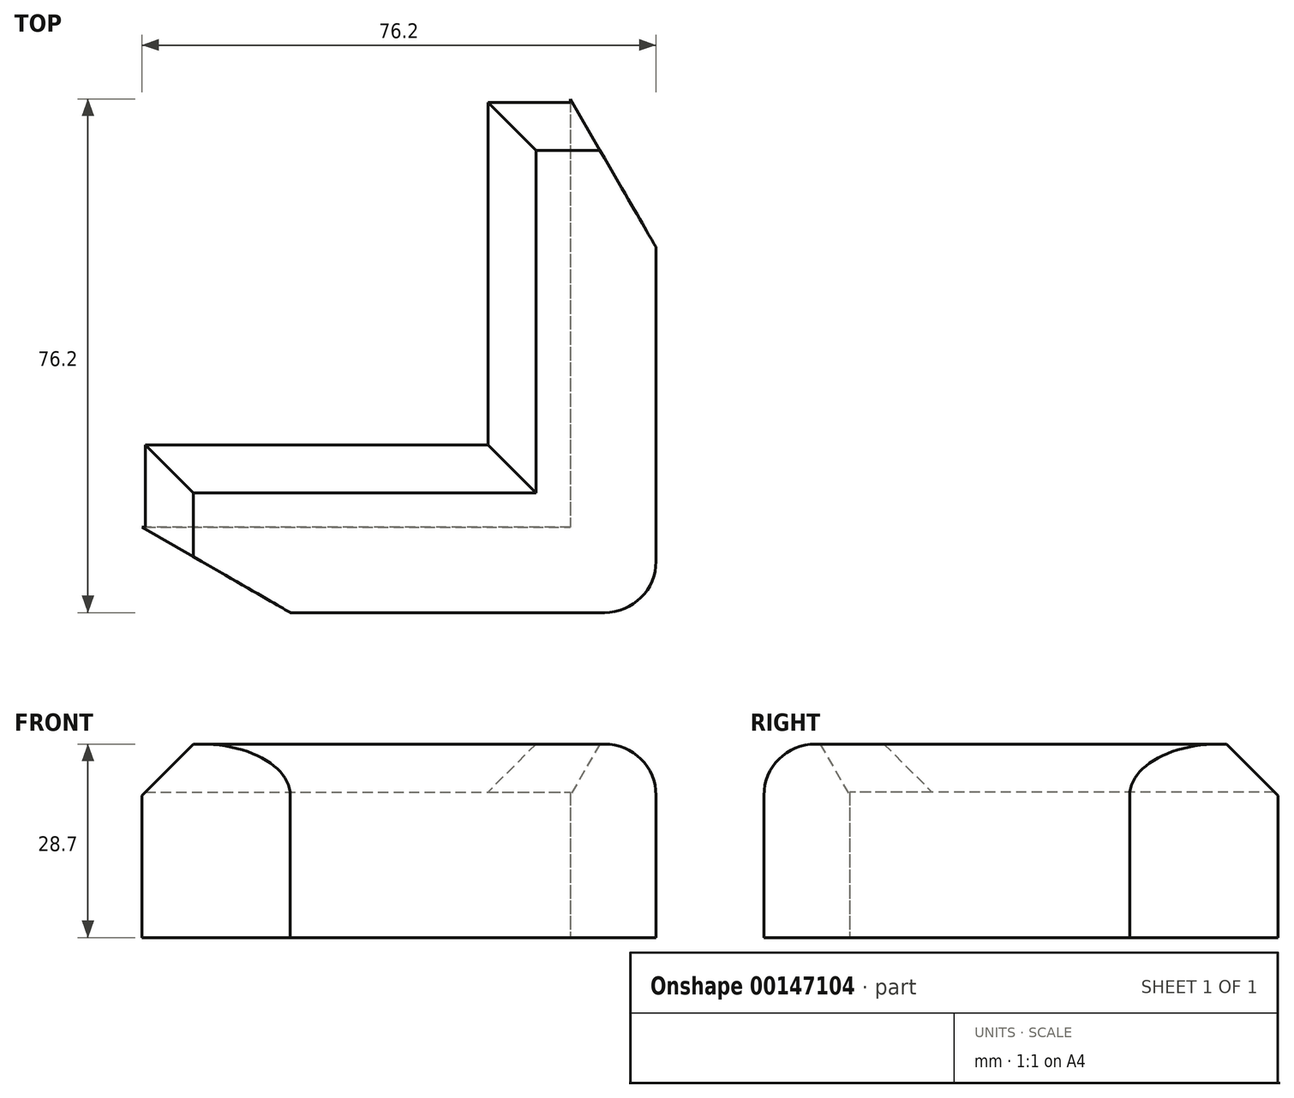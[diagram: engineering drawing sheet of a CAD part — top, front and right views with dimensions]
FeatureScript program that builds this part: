
annotation { "Feature Type Name" : "Feature", "Feature Type Description" : "" }
export const myFeature = defineFeature(function(context is Context, id is Id, definition is map)
    precondition{}
    {
        {
            var Q0;
            Q0=qCreatedBy(makeId("Front.planeOp"),FACE);
            var sketch = newSketch(context, id + "F0", { "sketchPlane" : qUnion([Q0])});
            skLineSegment(sketch, "E0.bottom", {"start": v(38.1, 14.35) * mm, "end": v(-38.1, 14.35) * mm});
            skLineSegment(sketch, "E0.top", {"start": v(38.1, -14.35) * mm, "end": v(-38.1, -14.35) * mm});
            skLineSegment(sketch, "E0.left", {"start": v(38.1, 14.35) * mm, "end": v(38.1, -14.35) * mm});
            skLineSegment(sketch, "E0.right", {"start": v(-38.1, 14.35) * mm, "end": v(-38.1, -14.35) * mm});
            skPoint(sketch, "E0.middle", {"position": v(0, 0) * mm});
            skLineSegment(sketch, "E1", {"start": v(25.4, 14.35) * mm, "end": v(25.4, -14.35) * mm});
            skLineSegment(sketch, "E2", {"start": v(-38.1, 7.24) * mm, "end": v(38.1, 7.24) * mm});
            skLineSegment(sketch, "E3", {"start": v(12.7, 14.35) * mm, "end": v(12.7, 7.24) * mm});
            skSolve(sketch);
        }
        {
            var Q0;
            {var subQ0=sQuery(id+"F0.wireOp",EDGE,"E0.right");var subQ1=sQuery(id+"F0.wireOp",EDGE,"E0.top");var subQ2=makeQuery(id+"F0.imprint","INTERSECT",VERTEX,{"derivedFrom":[subQ1,subQ0]});Q0=makeQuery(id+"F0.imprint","IMPRINT",FACE,{"disambiguationData":[TD([[makeQuery(id+"F0.imprint","IMPRINT",EDGE,{"disambiguationData":[TD([[subQ2,1.0]])],"derivedFrom":subQ1}),-1.0]])]});}
            extrude(context, id + "F1", {"entities" : qUnion([Q0]), "oppositeDirection" : true, "depth" : 12.7 * mm});
        }
        {
            var Q0;
            {var subQ0=sQuery(id+"F0.wireOp",EDGE,"E0.right");var subQ1=sQuery(id+"F0.wireOp",EDGE,"E0.bottom");var subQ2=makeQuery(id+"F0.imprint","INTERSECT",VERTEX,{"derivedFrom":[subQ1,subQ0]});Q0=makeQuery(id+"F0.imprint","IMPRINT",FACE,{"disambiguationData":[TD([[makeQuery(id+"F0.imprint","IMPRINT",EDGE,{"disambiguationData":[TD([[subQ2,1.0]])],"derivedFrom":subQ1}),1.0]])]});}
            extrude(context, id + "F2", {"entities" : qUnion([Q0]), "operationType" : NewBodyOperationType.ADD, "oppositeDirection" : true, "depth" : 25.4 * mm});
        }
        {
            var Q0;
            {var subQ0=sQuery(id+"F0.wireOp",EDGE,"E0.left");var subQ1=sQuery(id+"F0.wireOp",EDGE,"E0.top");var subQ2=makeQuery(id+"F0.imprint","INTERSECT",VERTEX,{"derivedFrom":[subQ1,subQ0]});Q0=makeQuery(id+"F0.imprint","IMPRINT",FACE,{"disambiguationData":[TD([[makeQuery(id+"F0.imprint","IMPRINT",EDGE,{"disambiguationData":[TD([[subQ2,-1.0]])],"derivedFrom":subQ1}),-1.0]])]});}
            var Q1;
            {var subQ0=sQuery(id+"F0.wireOp",EDGE,"E0.left");var subQ1=sQuery(id+"F0.wireOp",EDGE,"E0.bottom");var subQ2=makeQuery(id+"F0.imprint","INTERSECT",VERTEX,{"derivedFrom":[subQ1,subQ0]});Q1=makeQuery(id+"F0.imprint","IMPRINT",FACE,{"disambiguationData":[TD([[makeQuery(id+"F0.imprint","IMPRINT",EDGE,{"disambiguationData":[TD([[subQ2,-1.0]])],"derivedFrom":subQ1}),1.0]])]});}
            extrude(context, id + "F3", {"entities" : qUnion([Q0, Q1]), "operationType" : NewBodyOperationType.ADD, "oppositeDirection" : true, "depth" : 76.2 * mm});
        }
        {
            var Q0;
            {var subQ3=sQuery(id+"F0.wireOp",EDGE,"E3");Q0=makeQuery(id+"F0.imprint","IMPRINT",FACE,{"disambiguationData":[TD([[makeQuery(id+"F0.imprint","IMPRINT",EDGE,{"derivedFrom":subQ3}),1.0]])]});}
            extrude(context, id + "F4", {"entities" : qUnion([Q0]), "operationType" : NewBodyOperationType.ADD, "oppositeDirection" : true, "depth" : 76.2 * mm});
        }
        {
            var Q0;
            Q0=makeQuery(id+"F3.opExtrude","CAP_EDGE",EDGE,{"disambiguationData":[OSD([sQuery(id+"F0.wireOp",EDGE,"E0.left")])],"isStart":false});
            chamfer(context, id + "F5", {"entities" : qUnion([Q0]), "chamferType" : ChamferType.OFFSET_ANGLE, "width" : 12.7 * mm, "oppositeDirection" : false, "angle" : 60 * degree, "tangentPropagation" : true});
        }
        {
            var Q0;
            {var subQ0=sQuery(id+"F0.wireOp",EDGE,"E0.right");Q0=makeQuery(id+"F2.boolean.opBoolean","MERGE",EDGE,{"derivedFrom":[makeQuery(id+"F1.opExtrude","CAP_EDGE",EDGE,{"disambiguationData":[OSD([subQ0])],"isStart":true}),makeQuery(id+"F2.opExtrude","CAP_EDGE",EDGE,{"disambiguationData":[OSD([subQ0])],"isStart":true})]});}
            chamfer(context, id + "F6", {"entities" : qUnion([Q0]), "chamferType" : ChamferType.OFFSET_ANGLE, "width" : 12.7 * mm, "oppositeDirection" : true, "angle" : 60 * degree, "tangentPropagation" : true});
        }
        {
            var Q0;
            Q0=makeQuery(id+"F3.opExtrude","SWEPT_EDGE",EDGE,{"disambiguationData":[OSD([sQuery(id+"F0.wireOp",EDGE,"E0.bottom"),sQuery(id+"F0.wireOp",EDGE,"E0.left")])]});
            var Q1;
            {var subQ0=sQuery(id+"F0.wireOp",EDGE,"E0.bottom");Q1=makeQuery(id+"F4.boolean.opBoolean","MERGE",EDGE,{"derivedFrom":[makeQuery(id+"F2.opExtrude","CAP_EDGE",EDGE,{"disambiguationData":[OSD([subQ0])],"isStart":true}),makeQuery(id+"F3.opExtrude","CAP_EDGE",EDGE,{"disambiguationData":[OSD([subQ0])],"isStart":true}),makeQuery(id+"F4.opExtrude","CAP_EDGE",EDGE,{"disambiguationData":[OSD([subQ0])],"isStart":true})]});}
            var Q2;
            Q2=makeQuery(id+"F3.opExtrude","CAP_EDGE",EDGE,{"disambiguationData":[OSD([sQuery(id+"F0.wireOp",EDGE,"E0.left")])],"isStart":true});
            fillet(context, id + "F7", {"entities" : qUnion([Q0, Q1, Q2]), "radius" : 7.62 * mm, "tangentPropagation" : true, "allowEdgeOverflow" : false});
        }
        {
            var Q0;
            Q0=makeQuery(id+"F2.opExtrude","CAP_EDGE",EDGE,{"disambiguationData":[OSD([sQuery(id+"F0.wireOp",EDGE,"E0.bottom")])],"isStart":false});
            var Q1;
            Q1=makeQuery(id+"F4.opExtrude","SWEPT_EDGE",EDGE,{"disambiguationData":[OSD([sQuery(id+"F0.wireOp",EDGE,"E0.bottom"),sQuery(id+"F0.wireOp",EDGE,"E3")])]});
            var Q2;
            {var subQ0=sQuery(id+"F0.wireOp",EDGE,"E0.bottom");Q2=makeQuery(id+"F4.boolean.opBoolean","MERGE",EDGE,{"derivedFrom":[makeQuery(id+"F3.opExtrude","CAP_EDGE",EDGE,{"disambiguationData":[OSD([subQ0])],"isStart":false}),makeQuery(id+"F4.opExtrude","CAP_EDGE",EDGE,{"disambiguationData":[OSD([subQ0])],"isStart":false})]});}
            var Q3;
            Q3=makeQuery(id+"F2.opExtrude","SWEPT_EDGE",EDGE,{"disambiguationData":[OSD([sQuery(id+"F0.wireOp",EDGE,"E0.bottom"),sQuery(id+"F0.wireOp",EDGE,"E0.right")])]});
            chamfer(context, id + "F8", {"entities" : qUnion([Q0, Q1, Q2, Q3]), "width" : 7.62 * mm, "tangentPropagation" : true});
        }
    });
